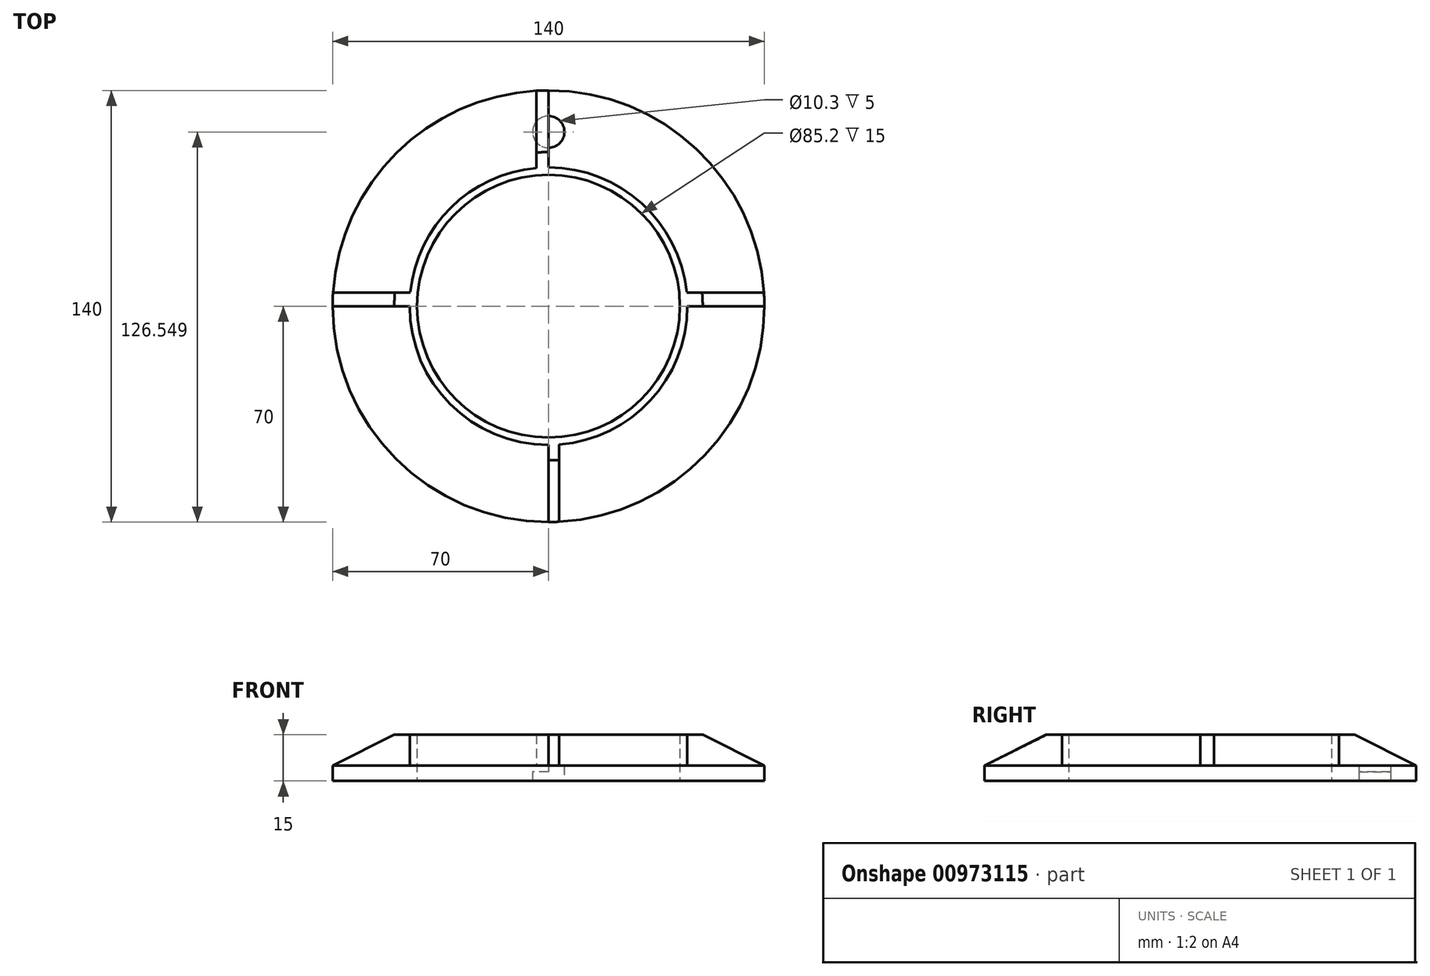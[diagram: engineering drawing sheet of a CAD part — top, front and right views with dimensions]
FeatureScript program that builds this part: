
annotation { "Feature Type Name" : "Feature", "Feature Type Description" : "" }
export const myFeature = defineFeature(function(context is Context, id is Id, definition is map)
    precondition{}
    {
        {
            var Q0;
            Q0=qCreatedBy(makeId("Top.planeOp"),FACE);
            var sketch = newSketch(context, id + "F0", { "sketchPlane" : qUnion([Q0])});
            skCircle(sketch, "E0", {"center": v(0, 0) * mm, "radius": 70 * mm});
            skCircle(sketch, "E1", {"center": v(0, 0) * mm, "radius": 42.6 * mm});
            skCircle(sketch, "E2", {"center": v(0, 0) * mm, "radius": 45 * mm});
            skCircle(sketch, "E3", {"center": v(0, 56.55) * mm, "radius": 5.15 * mm});
            skLineSegment(sketch, "E4", {"start": v(45, 0) * mm, "end": v(70, 0) * mm});
            skLineSegment(sketch, "E5", {"start": v(44.78, 4.48) * mm, "end": v(69.86, 4.48) * mm});
            skLineSegment(sketch, "E6", {"start": v(0, 45) * mm, "end": v(0, 70) * mm});
            skLineSegment(sketch, "E7", {"start": v(-3.9, 44.83) * mm, "end": v(-3.9, 69.9) * mm});
            skLineSegment(sketch, "E8", {"start": v(-45, 0) * mm, "end": v(-70, 0) * mm});
            skLineSegment(sketch, "E9", {"start": v(-44.78, 4.48) * mm, "end": v(-69.86, 4.48) * mm});
            skLineSegment(sketch, "E10", {"start": v(0, -45) * mm, "end": v(0, -70) * mm});
            skLineSegment(sketch, "E11", {"start": v(3.5, -44.86) * mm, "end": v(3.5, -69.91) * mm});
            skSolve(sketch);
        }
        {
            var Q0;
            Q0=makeQuery(id+"F0.imprint","IMPRINT",FACE,{"disambiguationData":[TD([[makeQuery(id+"F0.imprint","IMPRINT",EDGE,{"derivedFrom":sQuery(id+"F0.wireOp",EDGE,"E0")}),1.0]])]});
            var Q1;
            Q1=makeQuery(id+"F0.imprint","IMPRINT",FACE,{"disambiguationData":[TD([[makeQuery(id+"F0.imprint","IMPRINT",EDGE,{"derivedFrom":sQuery(id+"F0.wireOp",EDGE,"E3")}),1.0]])]});
            var Q2;
            {var subQ5=sQuery(id+"F0.wireOp",EDGE,"E9");Q2=makeQuery(id+"F0.imprint","IMPRINT",FACE,{"disambiguationData":[TD([[makeQuery(id+"F0.imprint","IMPRINT",EDGE,{"derivedFrom":subQ5}),-1.0]])]});}
            var Q3;
            {var subQ0=sQuery(id+"F0.wireOp",EDGE,"E7");var subQ1=sQuery(id+"F0.wireOp",EDGE,"E3");var subQ2=makeQuery(id+"F0.imprint","INTERSECT",VERTEX,{"disambiguationData":[OD(0.0)],"derivedFrom":[subQ1,subQ0]});Q3=makeQuery(id+"F0.imprint","IMPRINT",FACE,{"disambiguationData":[TD([[makeQuery(id+"F0.imprint","IMPRINT",EDGE,{"disambiguationData":[TD([[subQ2,-1.0]])],"derivedFrom":subQ1}),1.0]])]});}
            var Q4;
            {var subQ0=sQuery(id+"F0.wireOp",EDGE,"E6");var subQ1=sQuery(id+"F0.wireOp",EDGE,"E3");var subQ2=makeQuery(id+"F0.imprint","INTERSECT",VERTEX,{"disambiguationData":[OD(0.0)],"derivedFrom":[subQ1,subQ0]});Q4=makeQuery(id+"F0.imprint","IMPRINT",FACE,{"disambiguationData":[TD([[makeQuery(id+"F0.imprint","IMPRINT",EDGE,{"disambiguationData":[TD([[subQ2,1.0]])],"derivedFrom":subQ1}),1.0]])]});}
            var Q5;
            {var subQ0=sQuery(id+"F0.wireOp",EDGE,"E6");var subQ1=sQuery(id+"F0.wireOp",EDGE,"E2");var subQ2=makeQuery(id+"F0.imprint","INTERSECT",VERTEX,{"derivedFrom":[subQ1,subQ0]});Q5=makeQuery(id+"F0.imprint","IMPRINT",FACE,{"disambiguationData":[TD([[makeQuery(id+"F0.imprint","IMPRINT",EDGE,{"disambiguationData":[TD([[subQ2,-1.0]])],"derivedFrom":subQ1}),-1.0]])]});}
            var Q6;
            {var subQ0=sQuery(id+"F0.wireOp",EDGE,"E5");Q6=makeQuery(id+"F0.imprint","IMPRINT",FACE,{"disambiguationData":[TD([[makeQuery(id+"F0.imprint","IMPRINT",EDGE,{"derivedFrom":subQ0}),1.0]])]});}
            var Q7;
            Q7=makeQuery(id+"F0.imprint","IMPRINT",FACE,{"disambiguationData":[TD([[makeQuery(id+"F0.imprint","IMPRINT",EDGE,{"derivedFrom":sQuery(id+"F0.wireOp",EDGE,"E1")}),-1.0]])]});
            extrude(context, id + "F1", {"entities" : qUnion([Q0, Q1, Q2, Q3, Q4, Q5, Q6, Q7]), "depth" : 5 * mm, "offsetDistance" : 25 * mm});
        }
        {
            var Q0;
            Q0=makeQuery(id+"F0.imprint","IMPRINT",FACE,{"disambiguationData":[TD([[makeQuery(id+"F0.imprint","IMPRINT",EDGE,{"derivedFrom":sQuery(id+"F0.wireOp",EDGE,"E1")}),-1.0]])]});
            extrude(context, id + "F2", {"entities" : qUnion([Q0]), "operationType" : NewBodyOperationType.ADD, "depth" : 15 * mm, "offsetDistance" : 25 * mm});
        }
        {
            var Q0;
            Q0=makeQuery(id+"F0.imprint","IMPRINT",FACE,{"disambiguationData":[TD([[makeQuery(id+"F0.imprint","IMPRINT",EDGE,{"derivedFrom":sQuery(id+"F0.wireOp",EDGE,"E3")}),1.0]])]});
            var Q1;
            {var subQ0=sQuery(id+"F0.wireOp",EDGE,"E6");var subQ1=sQuery(id+"F0.wireOp",EDGE,"E3");var subQ2=makeQuery(id+"F0.imprint","INTERSECT",VERTEX,{"disambiguationData":[OD(0.0)],"derivedFrom":[subQ1,subQ0]});Q1=makeQuery(id+"F0.imprint","IMPRINT",FACE,{"disambiguationData":[TD([[makeQuery(id+"F0.imprint","IMPRINT",EDGE,{"disambiguationData":[TD([[subQ2,1.0]])],"derivedFrom":subQ1}),1.0]])]});}
            var Q2;
            {var subQ0=sQuery(id+"F0.wireOp",EDGE,"E7");var subQ1=sQuery(id+"F0.wireOp",EDGE,"E3");var subQ2=makeQuery(id+"F0.imprint","INTERSECT",VERTEX,{"disambiguationData":[OD(0.0)],"derivedFrom":[subQ1,subQ0]});Q2=makeQuery(id+"F0.imprint","IMPRINT",FACE,{"disambiguationData":[TD([[makeQuery(id+"F0.imprint","IMPRINT",EDGE,{"disambiguationData":[TD([[subQ2,-1.0]])],"derivedFrom":subQ1}),1.0]])]});}
            extrude(context, id + "F3", {"entities" : qUnion([Q0, Q1, Q2]), "operationType" : NewBodyOperationType.REMOVE, "depth" : 3 * mm, "offsetDistance" : 25 * mm});
        }
        {
            var Q0;
            {var subQ0=sQuery(id+"F0.wireOp",EDGE,"E10");Q0=makeQuery(id+"F0.imprint","IMPRINT",FACE,{"disambiguationData":[TD([[makeQuery(id+"F0.imprint","IMPRINT",EDGE,{"derivedFrom":subQ0}),1.0]])]});}
            var Q1;
            {var subQ0=sQuery(id+"F0.wireOp",EDGE,"E8");Q1=makeQuery(id+"F0.imprint","IMPRINT",FACE,{"disambiguationData":[TD([[makeQuery(id+"F0.imprint","IMPRINT",EDGE,{"derivedFrom":subQ0}),-1.0]])]});}
            var Q2;
            {var subQ0=sQuery(id+"F0.wireOp",EDGE,"E4");Q2=makeQuery(id+"F0.imprint","IMPRINT",FACE,{"disambiguationData":[TD([[makeQuery(id+"F0.imprint","IMPRINT",EDGE,{"derivedFrom":subQ0}),1.0]])]});}
            var Q3;
            {var subQ0=sQuery(id+"F0.wireOp",EDGE,"E7");var subQ1=sQuery(id+"F0.wireOp",EDGE,"E3");var subQ2=makeQuery(id+"F0.imprint","INTERSECT",VERTEX,{"disambiguationData":[OD(0.0)],"derivedFrom":[subQ1,subQ0]});Q3=makeQuery(id+"F0.imprint","IMPRINT",FACE,{"disambiguationData":[TD([[makeQuery(id+"F0.imprint","IMPRINT",EDGE,{"disambiguationData":[TD([[subQ2,1.0]])],"derivedFrom":subQ1}),1.0]])]});}
            var Q4;
            {var subQ0=sQuery(id+"F0.wireOp",EDGE,"E6");var subQ1=sQuery(id+"F0.wireOp",EDGE,"E0");var subQ2=makeQuery(id+"F0.imprint","INTERSECT",VERTEX,{"derivedFrom":[subQ1,subQ0]});Q4=makeQuery(id+"F0.imprint","IMPRINT",FACE,{"disambiguationData":[TD([[makeQuery(id+"F0.imprint","IMPRINT",EDGE,{"disambiguationData":[TD([[subQ2,-1.0]])],"derivedFrom":subQ1}),1.0]])]});}
            var Q5;
            {var subQ0=sQuery(id+"F0.wireOp",EDGE,"E6");var subQ1=sQuery(id+"F0.wireOp",EDGE,"E2");var subQ2=makeQuery(id+"F0.imprint","INTERSECT",VERTEX,{"derivedFrom":[subQ1,subQ0]});Q5=makeQuery(id+"F0.imprint","IMPRINT",FACE,{"disambiguationData":[TD([[makeQuery(id+"F0.imprint","IMPRINT",EDGE,{"disambiguationData":[TD([[subQ2,-1.0]])],"derivedFrom":subQ1}),-1.0]])]});}
            extrude(context, id + "F4", {"entities" : qUnion([Q0, Q1, Q2, Q3, Q4, Q5]), "operationType" : NewBodyOperationType.ADD, "depth" : 15 * mm, "offsetDistance" : 25 * mm, "hasSecondDirection" : true, "secondDirectionOppositeDirection" : false, "secondDirectionDepth" : 5 * mm});
        }
        {
            var Q0;
            {var subQ0=sQuery(id+"F0.wireOp",EDGE,"E0");Q0=makeQuery(id+"F4.opExtrude","CAP_EDGE",EDGE,{"disambiguationData":[OSD([subQ0]),TDD([makeQuery(id+"F0.imprint","IMPRINT",EDGE,{"disambiguationData":[TD([[makeQuery(id+"F0.imprint","INTERSECT",VERTEX,{"derivedFrom":[subQ0,sQuery(id+"F0.wireOp",EDGE,"E4")]}),-1.0]])],"derivedFrom":subQ0})])],"isStart":false});}
            var Q1;
            {var subQ0=sQuery(id+"F0.wireOp",EDGE,"E0");Q1=makeQuery(id+"F4.opExtrude","CAP_EDGE",EDGE,{"disambiguationData":[OSD([subQ0]),TDD([makeQuery(id+"F0.imprint","IMPRINT",EDGE,{"disambiguationData":[TD([[makeQuery(id+"F0.imprint","INTERSECT",VERTEX,{"derivedFrom":[subQ0,sQuery(id+"F0.wireOp",EDGE,"E10")]}),-1.0]])],"derivedFrom":subQ0})])],"isStart":false});}
            var Q2;
            {var subQ0=sQuery(id+"F0.wireOp",EDGE,"E0");Q2=makeQuery(id+"F4.opExtrude","CAP_EDGE",EDGE,{"disambiguationData":[OSD([subQ0]),TDD([makeQuery(id+"F0.imprint","IMPRINT",EDGE,{"disambiguationData":[TD([[makeQuery(id+"F0.imprint","INTERSECT",VERTEX,{"derivedFrom":[subQ0,sQuery(id+"F0.wireOp",EDGE,"E8")]}),1.0]])],"derivedFrom":subQ0})])],"isStart":false});}
            var Q3;
            {var subQ0=sQuery(id+"F0.wireOp",EDGE,"E0");Q3=makeQuery(id+"F4.opExtrude","CAP_EDGE",EDGE,{"disambiguationData":[OSD([subQ0]),TDD([makeQuery(id+"F0.imprint","IMPRINT",EDGE,{"disambiguationData":[TD([[makeQuery(id+"F0.imprint","INTERSECT",VERTEX,{"derivedFrom":[subQ0,sQuery(id+"F0.wireOp",EDGE,"E6")]}),-1.0]])],"derivedFrom":subQ0})])],"isStart":false});}
            chamfer(context, id + "F5", {"entities" : qUnion([Q0, Q1, Q2, Q3]), "chamferType" : ChamferType.TWO_OFFSETS, "width1" : 20 * mm, "oppositeDirection" : false, "width2" : 10 * mm, "tangentPropagation" : true});
        }
    });
